# Revit family: Lighting_Sconce_HalfRound
name_source: partatom
category: Lighting Fixtures
units: mm (PartAtom-declared; Revit-internal decimal feet)

## family parameters
Always vertical = Yes
Classification Number = 23.80.70.11
Cut with Voids When Loaded = No
Host = Wall
Light Source = Yes
Maintain Annotation Orientation = No
Part Type = Normal
Room Calculation Point = No
Round Connector Dimension = Use Diameter
Shared = No

## types (4) — shared parameters
Assembly Code = D5020220
Bracket Material = ARCAT - Metal, Brass
Color Filter = 16777215
Construction Details = http://www.arcat.com
Current (Amps) = 0.5
Default Elevation = 0' - 0"
Diffuser Material = ARCAT - Glass, Frosted, Deep Amber
Dimming Lamp Color Temperature Shift = <None>
Dist From Wall = 0' - 2"
Emit from Line Length = 3' - 3"
Expected Lifespan (Years) = 15
Green Building-LEED = http://www.arcat.com
Installation Phase = Finish Electrical
Keynote = 16510
Lamp = Incandescent - Max 100W
Light Source Symbol Size = 2' - 0"
Maintenance Schedule (Months) = 6
Manufacturer = Generic
Manufacturer Fax = (203) 929-2444
Manufacturer Website = http://www.arcat.com
Model = Generic
Placement Height = 7' - 0"
Product Data = http://www.arcat.com
Product Properties = http://www.arcat.com
Specification = http://www.arcat.com
Spread = 0' - 6"
Wall Plate Material = ARCAT - Metal, Brass
Warranty Duration (Years) = 1
Width = 0' - 10"

## per-type parameters (varying)
| type | Bulb | Description | Wattage Comments |
| 60 Watt Fixture | Incandescent_Bulb : 60 Watt Incandescent | 60 Watt Wall Sconce | 60 |
| 40 Watt Fixture | Incandescent_Bulb : 40 Watt Incandescent | 40 Watt Wall Sconce | 40 |
| 75 Watt Fixture | Incandescent_Bulb : 75 Watt Incandescent | 75 Watt Wall Sconce | 75 |
| 100 Watt Fixture | Incandescent_Bulb : 100 Watt Incandescent | 100 Watt Wall Sconce | 100 |

## geometry (parser evidence)
native form markers: Sweep x6
no freeform markers — native parametric forms only
